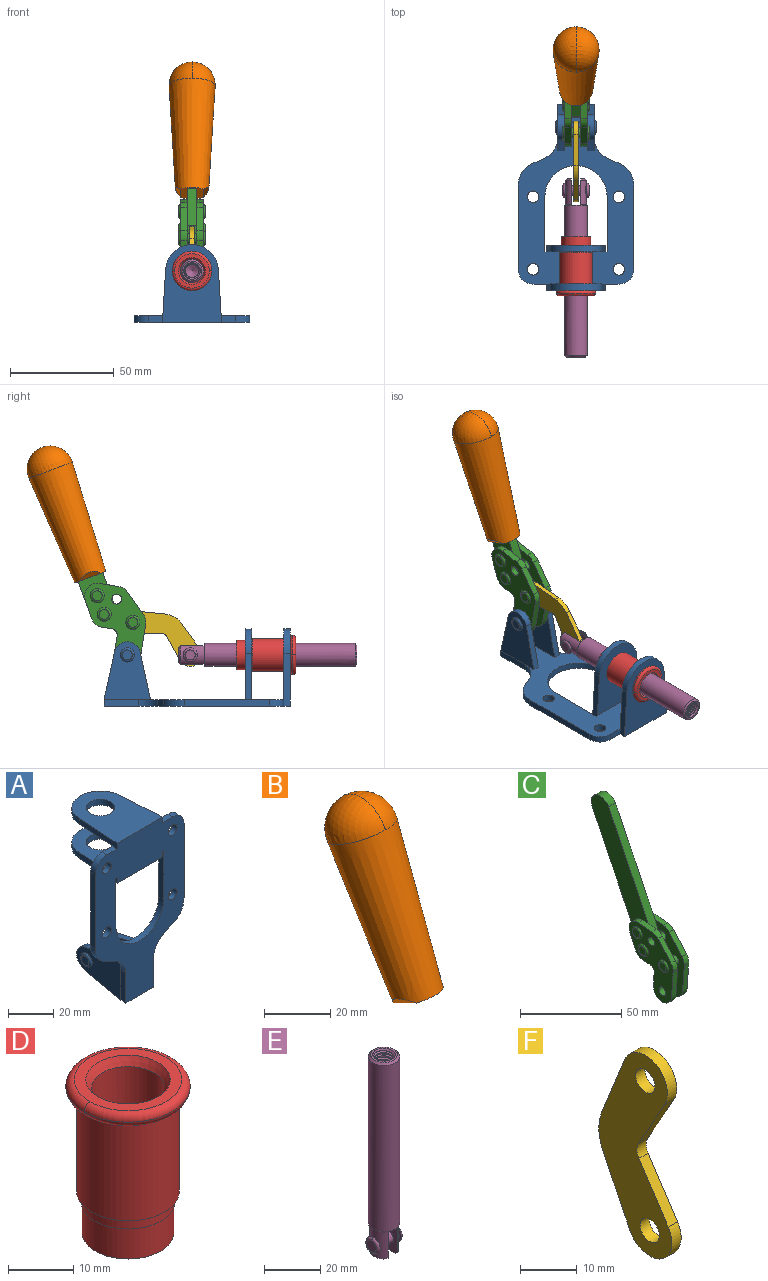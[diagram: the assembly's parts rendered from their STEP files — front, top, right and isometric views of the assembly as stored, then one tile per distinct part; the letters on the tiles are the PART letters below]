
ASSEMBLY  parts=6 mates=6
PART A: 55 faces, bbox 55.7x37.4x89.8 mm
  f0: torus R=2.41mm, axis (-1,0,0), area 15mm2, adj f11,f15,f25
  f1: torus R=2.41mm, axis (-1,0,0), area 15mm2, adj f10,f12,f22
  f2: cylinder r=2.78mm len=5.56mm, axis (0,-1,0), area 54.2mm2, adj f30,f54
  f3: cylinder r=14.99mm len=29.97mm, axis (0,-1,0), area 145.9mm2, adj f30,f49,f53,f54
  f4: cylinder r=2.78mm len=5.56mm, axis (0,-1,0), area 54.2mm2, adj f30,f54
  f5: cylinder r=2.78mm len=5.56mm, axis (0,-1,0), area 54.2mm2, adj f30,f54
  f6: cylinder r=2.78mm len=5.56mm, axis (0,-1,0), area 54.2mm2, adj f30,f54
  f7: cylinder r=6.35mm len=12.7mm, axis (0,0,1), area 123.6mm2, adj f27,f51
  f8: cylinder r=6.35mm len=12.7mm, axis (0,0,-1), area 124.7mm2, adj f21,f35
  f9: cylinder r=2.41mm len=11.18mm, axis (-1,0,0), area 169.4mm2, adj f16,f19
  f10: plane 4.83x4.83mm, normal (1,0,0), area 18.3mm2, adj f1,f12
  f11: plane 4.83x4.83mm, normal (-1,0,0), area 18.3mm2, adj f0,f15
  f12: torus R=2.41mm, axis (-1,0,0), area 15mm2, adj f1,f10,f22
  f13: cylinder r=6.35mm len=12.41mm, axis (1,0,0), area 53.4mm2, adj f18,f19,f22,f23
  f14: cylinder r=6.35mm len=12.41mm, axis (-1,0,0), area 53.4mm2, adj f16,f17,f24,f25
  f15: torus R=2.41mm, axis (-1,0,0), area 15mm2, adj f0,f11,f25
  f16: plane 27.86x22.35mm, normal (1,0,0), area 425.4mm2, adj f9,f14,f17,f24,f30
  f17: plane 22.86x4.97mm, normal (0,0.21,0.98), area 72.5mm2, adj f14,f16,f25,f30
  f18: plane 22.86x4.97mm, normal (0,0.21,0.98), area 72.5mm2, adj f13,f19,f22,f30
  f19: plane 27.86x22.35mm, normal (-1,0,0), area 425.4mm2, adj f9,f13,f18,f23,f30
  f20: cylinder r=12.7mm len=25.35mm, axis (0,0,-1), area 119.8mm2, adj f21,f34,f35,f36
  f21: plane 34.21x28.07mm, normal (0,0,-1), area 702.4mm2, adj f8,f20,f30,f34,f36
  f22: plane 27.96x22.45mm, normal (1,0,0), area 407.2mm2, adj f1,f12,f13,f18,f23,f30,f42,f43
  f23: plane 22.86x4.97mm, normal (0,0.21,-0.98), area 72.5mm2, adj f13,f19,f22,f44
  f24: plane 22.86x4.97mm, normal (0,0.21,-0.98), area 72.5mm2, adj f14,f16,f25,f44
  f25: plane 27.86x22.35mm, normal (-1,0,0), area 407.1mm2, adj f0,f14,f15,f17,f24,f30,f45,f46
  f26: plane 3.1x0.95mm, normal (0,0,-1), area 2.7mm2, adj f30,f49,f50,f54
  f27: plane 34.21x28.07mm, normal (0,0,1), area 702.4mm2, adj f7,f28,f30,f50,f52
  f28: cylinder r=12.7mm len=25.35mm, axis (0,0,1), area 118.8mm2, adj f27,f50,f51,f52
  f29: plane 3.1x0.95mm, normal (0,0,-1), area 2.7mm2, adj f30,f52,f53,f54
  f30: plane 86.54x55.63mm, normal (0,1,0), area 2362.9mm2, adj f2,f3,f4,f5,f6,f16,f17,f18
  f31: plane 40.56x3.1mm, normal (-1,0,0), area 125.7mm2, adj f30,f32,f48,f54
  f32: cylinder r=7.11mm len=7.11mm, axis (0,-1,0), area 34.6mm2, adj f30,f31,f33,f54
  f33: plane 6.67x3.1mm, normal (0,0,1), area 20.4mm2, adj f30,f32,f34,f54
  f34: plane 25.39x3.13mm, normal (-1,0.06,0), area 79.5mm2, adj f20,f21,f33,f35,f54
  f35: plane 37.31x28.45mm, normal (0,0,1), area 789.9mm2, adj f8,f20,f34,f36,f54
  f36: plane 25.39x3.13mm, normal (1,0.06,0), area 79.5mm2, adj f20,f21,f35,f37,f54
  f37: plane 6.67x3.1mm, normal (0,0,1), area 20.4mm2, adj f30,f36,f38,f54
  f38: cylinder r=7.11mm len=7.11mm, axis (0,-1,0), area 34.6mm2, adj f30,f37,f39,f54
  f39: plane 40.56x3.1mm, normal (1,0,0), area 125.7mm2, adj f30,f38,f40,f54
  f40: cylinder r=11.18mm len=10.16mm, axis (0,-1,0), area 39.5mm2, adj f30,f39,f41,f54
  f41: plane 6.09x3.1mm, normal (0.42,0,-0.91), area 20.8mm2, adj f30,f40,f42,f54
  f42: cylinder r=11.18mm len=9.41mm, axis (0,-1,0), area 37.2mm2, adj f22,f30,f41,f43,f54
  f43: plane 16.5x3.1mm, normal (1,0,0), area 51.1mm2, adj f22,f42,f44,f54
  f44: plane 17.37x3.1mm, normal (0,0,-1), area 53.8mm2, adj f23,f24,f30,f43,f45,f54
  f45: plane 16.5x3.1mm, normal (-1,0,0), area 51.1mm2, adj f25,f44,f46,f54
  f46: cylinder r=11.18mm len=9.41mm, axis (0,-1,0), area 37.2mm2, adj f25,f30,f45,f47,f54
  f47: plane 6.09x3.1mm, normal (-0.42,0,-0.91), area 20.8mm2, adj f30,f46,f48,f54
  f48: cylinder r=11.18mm len=10.16mm, axis (0,-1,0), area 39.5mm2, adj f30,f31,f47,f54
  f49: plane 26.54x3.1mm, normal (-1,0,0), area 82.3mm2, adj f3,f26,f30,f54
  f50: plane 25.39x3.1mm, normal (1,0.06,0), area 78.8mm2, adj f26,f27,f28,f51,f54
  f51: plane 37.31x28.45mm, normal (0,0,-1), area 789.9mm2, adj f7,f28,f50,f52,f54
  f52: plane 25.39x3.1mm, normal (-1,0.06,0), area 78.8mm2, adj f27,f28,f29,f51,f54
  f53: plane 26.54x3.1mm, normal (1,0,0), area 82.3mm2, adj f3,f29,f30,f54
  f54: plane 89.66x55.63mm, normal (0,-1,0), area 2678.5mm2, adj f2,f3,f4,f5,f6,f26,f29,f31
PART B: 11 faces, bbox 22.3x42.6x64.5 mm
  f0: sphere r=11.13mm, area 411.4mm2, adj f1,f8
  f1: cone r=11.11mm half-angle=3.3deg, axis (0,0.44,0.9), area 3251.8mm2, adj f0,f7,f8,f9,f10
  f2: cylinder r=6.16mm len=11.7mm, axis (1,0,0), area 89.5mm2, adj f3,f4,f5,f6
  f3: plane 60.23x36.75mm, normal (-1,0,0), area 763.6mm2, adj f2,f4,f6,f10
  f4: plane 51.37x25.05mm, normal (0,0.9,-0.44), area 264.2mm2, adj f2,f3,f5,f10
  f5: plane 60.23x36.75mm, normal (1,0,0), area 763.6mm2, adj f2,f4,f6,f10
  f6: plane 51.37x25.05mm, normal (0,-0.9,0.44), area 264.2mm2, adj f2,f3,f5,f10
  f7: plane 9.95x5.95mm, normal (0.71,-0.31,-0.64), area 25.8mm2, adj f1,f10
  f8: sphere r=11.13mm, area 411.4mm2, adj f0,f1
  f9: plane 9.95x5.95mm, normal (-0.71,-0.31,-0.64), area 25.8mm2, adj f1,f10
  f10: plane 14.27x11.38mm, normal (0,-0.44,-0.9), area 106.7mm2, adj f1,f3,f4,f5,f6,f7,f9
PART C: 59 faces, bbox 12.9x60.2x99.6 mm
  f0: torus R=2.39mm, axis (-1,0,0), area 14.9mm2, adj f20,f43,f51
  f1: torus R=2.39mm, axis (-1,0,0), area 14.9mm2, adj f19,f42,f51
  f2: torus R=2.39mm, axis (-1,0,0), area 14.9mm2, adj f18,f35,f51
  f3: torus R=2.39mm, axis (-1,0,0), area 14.9mm2, adj f14,f17,f23
  f4: torus R=2.39mm, axis (-1,0,0), area 14.9mm2, adj f13,f16,f23
  f5: torus R=2.39mm, axis (-1,0,0), area 14.9mm2, adj f12,f15,f23
  f6: cylinder r=2.39mm len=4.78mm, axis (1,0,0), area 46.5mm2, adj f48,f50,f51
  f7: cylinder r=2.39mm len=4.78mm, axis (1,0,0), area 46.5mm2, adj f50,f51
  f8: cylinder r=6.35mm len=12.68mm, axis (1,0,0), area 61.8mm2, adj f38,f39,f50,f51
  f9: cylinder r=2.39mm len=4.78mm, axis (-1,0,0), area 70.5mm2, adj f46,f50
  f10: cylinder r=2.39mm len=4.78mm, axis (-1,0,0), area 46.5mm2, adj f23,f45,f46
  f11: cylinder r=2.39mm len=4.78mm, axis (-1,0,0), area 46.5mm2, adj f23,f46
  f12: plane 4.78x4.78mm, normal (1,0,0), area 17.9mm2, adj f5,f15
  f13: plane 4.78x4.78mm, normal (1,0,0), area 17.9mm2, adj f4,f16
  f14: plane 4.78x4.78mm, normal (1,0,0), area 17.9mm2, adj f3,f17
  f15: torus R=2.39mm, axis (-1,0,0), area 14.9mm2, adj f5,f12,f23
  f16: torus R=2.39mm, axis (-1,0,0), area 14.9mm2, adj f4,f13,f23
  f17: torus R=2.39mm, axis (-1,0,0), area 14.9mm2, adj f3,f14,f23
  f18: plane 4.78x4.78mm, normal (-1,0,0), area 17.9mm2, adj f2,f35
  f19: plane 4.78x4.78mm, normal (-1,0,0), area 17.9mm2, adj f1,f42
  f20: plane 4.78x4.78mm, normal (-1,0,0), area 17.9mm2, adj f0,f43
  f21: plane 2.26x0.2mm, normal (1,0,0), area 0.2mm2, adj f31,f44
  f22: plane 2.26x0.2mm, normal (-1,0,0), area 0.2mm2, adj f41,f44
  f23: plane 39.37x30.77mm, normal (1,0,0), area 565.5mm2, adj f3,f4,f5,f10,f11,f15,f16,f17
  f24: cylinder r=6.1mm len=4.15mm, axis (-1,0,0), area 14.7mm2, adj f23,f25,f32,f46
  f25: plane 10.25x9.01mm, normal (0,-0.75,0.66), area 42.3mm2, adj f23,f24,f26,f46
  f26: cylinder r=6.35mm len=4.64mm, axis (-1,0,0), area 15.6mm2, adj f23,f25,f27,f46
  f27: plane 15.84x3.1mm, normal (0,-1,-0.07), area 49.2mm2, adj f23,f26,f28,f46
  f28: cylinder r=6.35mm len=12.68mm, axis (-1,0,0), area 61.8mm2, adj f23,f27,f29,f46
  f29: plane 8.11x3.1mm, normal (0,1,0.07), area 25.2mm2, adj f23,f28,f30,f46
  f30: cylinder r=3.05mm len=3.25mm, axis (-1,0,0), area 14.8mm2, adj f23,f29,f31,f46
  f31: plane 5.99x3.1mm, normal (0,0.07,-1), area 18.6mm2, adj f21,f23,f30,f44,f46
  f32: plane 9.5x3.1mm, normal (0,-0.07,1), area 29.5mm2, adj f23,f24,f33,f46,f47
  f33: cylinder r=6.1mm len=8.63mm, axis (-1,0,0), area 39.1mm2, adj f23,f32,f34,f47
  f34: plane 8.65x3.96mm, normal (0,0.91,-0.42), area 29.5mm2, adj f23,f33,f44,f47
  f35: torus R=2.39mm, axis (-1,0,0), area 14.9mm2, adj f2,f18,f51
  f36: plane 10.25x9.01mm, normal (0,-0.75,0.66), area 42.3mm2, adj f37,f49,f50,f51
  f37: cylinder r=6.35mm len=4.64mm, axis (1,0,0), area 15.6mm2, adj f36,f38,f50,f51
  f38: plane 15.84x3.1mm, normal (0,-1,-0.07), area 49.2mm2, adj f8,f37,f50,f51
  f39: plane 8.11x3.1mm, normal (0,1,0.07), area 25.2mm2, adj f8,f40,f50,f51
  f40: cylinder r=3.05mm len=3.25mm, axis (1,0,0), area 14.8mm2, adj f39,f41,f50,f51
  f41: plane 5.99x3.1mm, normal (0,0.07,-1), area 18.6mm2, adj f22,f40,f44,f50,f51
  f42: torus R=2.39mm, axis (-1,0,0), area 14.9mm2, adj f1,f19,f51
  f43: torus R=2.39mm, axis (-1,0,0), area 14.9mm2, adj f0,f20,f51
  f44: cylinder r=6.35mm len=12.12mm, axis (-1,0,0), area 128.9mm2, adj f21,f22,f23,f31,f34,f41,f46,f47
  f45: plane 2.65x1.35mm, normal (1,0,0), area 1mm2, adj f10,f55
  f46: plane 39.08x20.42mm, normal (-1,0,0), area 412.5mm2, adj f9,f10,f11,f24,f25,f26,f27,f28
  f47: plane 77.62x39.82mm, normal (1,0,0), area 850mm2, adj f32,f33,f34,f44,f53,f54,f55
  f48: plane 2.65x1.35mm, normal (-1,0,0), area 1mm2, adj f6,f55
  f49: cylinder r=6.1mm len=4.15mm, axis (1,0,0), area 14.7mm2, adj f36,f50,f51,f56
  f50: plane 39.08x20.42mm, normal (1,0,0), area 412.5mm2, adj f6,f7,f8,f9,f36,f37,f38,f39
  f51: plane 39.37x30.77mm, normal (-1,0,0), area 565.5mm2, adj f0,f1,f2,f6,f7,f8,f35,f36
  f52: plane 8.65x3.96mm, normal (0,0.91,-0.42), area 29.5mm2, adj f44,f51,f57,f58
  f53: plane 68.49x33.4mm, normal (0,0.9,-0.44), area 358.1mm2, adj f44,f47,f54,f58
  f54: cylinder r=6.35mm len=12.06mm, axis (1,0,0), area 93.7mm2, adj f47,f53,f55,f58
  f55: plane 68.49x33.4mm, normal (0,-0.9,0.44), area 358.1mm2, adj f44,f45,f46,f47,f48,f50,f54,f58
  f56: plane 9.5x3.1mm, normal (0,-0.07,1), area 29.5mm2, adj f49,f50,f51,f57,f58
  f57: cylinder r=6.1mm len=8.63mm, axis (1,0,0), area 39.1mm2, adj f51,f52,f56,f58
  f58: plane 77.62x39.82mm, normal (-1,0,0), area 850mm2, adj f44,f52,f53,f54,f55,f56,f57
PART D: 15 faces, bbox 20.6x20.6x28.7 mm
  f0: torus R=8.26mm, axis (0,0,1), area 56.8mm2, adj f1,f10,f12
  f1: torus R=8.26mm, axis (0,0,1), area 56.8mm2, adj f0,f6,f13
  f2: cylinder r=5.59mm len=25.91mm, axis (0,0,1), area 909.6mm2, adj f3,f4
  f3: cone r=6.86mm half-angle=45deg, axis (0,0,-1), area 70.2mm2, adj f2,f14
  f4: cone r=6.47mm half-angle=30deg, axis (0,0,1), area 66.7mm2, adj f2,f13
  f5: cylinder r=7.04mm len=14.07mm, axis (0,0,1), area 252.6mm2, adj f11,f14
  f6: torus R=8.26mm, axis (0,0,1), area 56.8mm2, adj f1,f12,f13
  f7: cylinder r=7.16mm len=14.33mm, axis (0,0,1), area 91.5mm2, adj f9,f11
  f8: cylinder r=7.86mm len=18.42mm, axis (0,0,1), area 909.6mm2, adj f9,f10
  f9: plane 15.72x15.72mm, normal (0,0,-1), area 33mm2, adj f7,f8
  f10: plane 16.51x16.51mm, normal (0,0,-1), area 19.9mm2, adj f0,f8,f12
  f11: plane 14.33x14.33mm, normal (0,0,-1), area 5.7mm2, adj f5,f7
  f12: torus R=8.26mm, axis (0,0,1), area 56.8mm2, adj f0,f6,f10
  f13: plane 16.51x16.51mm, normal (0,0,1), area 82.7mm2, adj f1,f4,f6
  f14: plane 14.07x14.07mm, normal (0,0,-1), area 7.8mm2, adj f3,f5
PART E: 48 faces, bbox 12.6x11.1x86.1 mm
  f0: torus R=2.41mm, axis (-1,0,0), area 15mm2, adj f30,f32,f34
  f1: torus R=2.41mm, axis (-1,0,0), area 15mm2, adj f29,f31,f33
  f2: cylinder r=5.54mm len=72.39mm, axis (0,0,1), area 2518.5mm2, adj f3,f4,f42,f43
  f3: cone r=5.54mm half-angle=45deg, axis (0,0,1), area 7.6mm2, adj f2,f5,f41
  f4: cone r=5.54mm half-angle=45deg, axis (0,0,-1), area 34.9mm2, adj f2,f39
  f5: cylinder r=5.08mm len=11.48mm, axis (0,0,1), area 108.3mm2, adj f3,f7,f8,f41
  f6: cylinder r=2.41mm len=4.83mm, axis (-1,0,0), area 71.2mm2, adj f40,f41
  f7: cylinder r=2.41mm len=4.83mm, axis (-1,0,0), area 7.6mm2, adj f5,f34
  f8: cone r=5.08mm half-angle=45deg, axis (0,0,1), area 10.6mm2, adj f5,f37,f41
  f9: cone r=3.98mm half-angle=45deg, axis (0,0,1), area 17.6mm2, adj f27,f39,f45,f46,f47
  f10: cylinder r=2.41mm len=4.83mm, axis (-1,0,0), area 7.6mm2, adj f33,f38
  f11: cylinder r=3.2mm len=6.4mm, axis (0,0,1), area 78.4mm2, adj f12,f28,f44,f45,f47
  f12: cylinder r=3.2mm len=6.4mm, axis (0,0,1), area 10.5mm2, adj f11,f13,f45,f47
  f13: cylinder r=3.2mm len=6.4mm, axis (0,0,1), area 10.5mm2, adj f12,f14,f45,f47
  f14: cylinder r=3.2mm len=6.4mm, axis (0,0,1), area 10.5mm2, adj f13,f15,f45,f47
  f15: cylinder r=3.2mm len=6.4mm, axis (0,0,1), area 10.5mm2, adj f14,f16,f45,f47
  f16: cylinder r=3.2mm len=6.4mm, axis (0,0,1), area 10.5mm2, adj f15,f17,f45,f47
  f17: cylinder r=3.2mm len=6.4mm, axis (0,0,1), area 10.5mm2, adj f16,f18,f45,f47
  f18: cylinder r=3.2mm len=6.4mm, axis (0,0,1), area 10.5mm2, adj f17,f19,f45,f47
  f19: cylinder r=3.2mm len=6.4mm, axis (0,0,1), area 10.5mm2, adj f18,f20,f45,f47
  f20: cylinder r=3.2mm len=6.4mm, axis (0,0,1), area 10.5mm2, adj f19,f21,f45,f47
  f21: cylinder r=3.2mm len=6.4mm, axis (0,0,1), area 10.5mm2, adj f20,f22,f45,f47
  f22: cylinder r=3.2mm len=6.4mm, axis (0,0,1), area 10.5mm2, adj f21,f23,f45,f47
  f23: cylinder r=3.2mm len=6.4mm, axis (0,0,1), area 10.5mm2, adj f22,f24,f45,f47
  f24: cylinder r=3.2mm len=6.4mm, axis (0,0,1), area 10.5mm2, adj f23,f25,f45,f47
  f25: cylinder r=3.2mm len=6.4mm, axis (0,0,1), area 10.5mm2, adj f24,f26,f45,f47
  f26: cylinder r=3.2mm len=6.4mm, axis (0,0,1), area 10.5mm2, adj f25,f27,f45,f47
  f27: cylinder r=3.2mm len=6.4mm, axis (0,0,1), area 7.4mm2, adj f9,f26,f45,f47
  f28: cone r=3.2mm half-angle=60deg, axis (0,0,1), area 37.2mm2, adj f11
  f29: plane 4.83x4.83mm, normal (-1,0,0), area 18.3mm2, adj f1,f31
  f30: plane 4.83x4.83mm, normal (1,0,0), area 18.3mm2, adj f0,f32
  f31: torus R=2.41mm, axis (-1,0,0), area 15mm2, adj f1,f29,f33
  f32: torus R=2.41mm, axis (-1,0,0), area 15mm2, adj f0,f30,f34
  f33: plane 6.83x6.83mm, normal (1,0,0), area 18.3mm2, adj f1,f10,f31
  f34: plane 6.83x6.83mm, normal (-1,0,0), area 18.3mm2, adj f0,f7,f32
  f35: cone r=5.08mm half-angle=45deg, axis (0,0,1), area 10.6mm2, adj f36,f38,f40
  f36: plane 7.25x1.97mm, normal (0,0,-1), area 10mm2, adj f35,f40
  f37: plane 7.25x1.97mm, normal (0,0,-1), area 10mm2, adj f8,f41
  f38: cylinder r=5.08mm len=11.48mm, axis (0,0,1), area 108.3mm2, adj f10,f35,f40,f42
  f39: plane 9.55x9.55mm, normal (0,0,1), area 22mm2, adj f4,f9
  f40: plane 12.76x10.09mm, normal (1,0,0), area 95.7mm2, adj f6,f35,f36,f38,f42,f43
  f41: plane 12.76x10.09mm, normal (-1,0,0), area 95.7mm2, adj f3,f5,f6,f8,f37,f43
  f42: cone r=5.54mm half-angle=45deg, axis (0,0,1), area 7.6mm2, adj f2,f38,f40
  f43: plane 11.07x4.7mm, normal (0,0,-1), area 50.4mm2, adj f2,f40,f41
  f44: plane 0.89x0.62mm, normal (-1,0,0), area 0.3mm2, adj f11,f45,f46,f47
  f45: bspline ~24.8x7.63mm, area 266.6mm2, adj f9,f11,f12,f13,f14,f15,f16,f17
  f46: bspline ~24.87x7.63mm, area 73.6mm2, adj f9,f44,f45,f47
  f47: bspline ~24.98x7.63mm, area 272.5mm2, adj f9,f11,f12,f13,f14,f15,f16,f17
PART F: 12 faces, bbox 2.3x18.2x42.8 mm
  f0: cylinder r=2.4mm len=4.8mm, axis (1,0,0), area 34.9mm2, adj f4,f11
  f1: cylinder r=10.41mm len=8.47mm, axis (1,0,0), area 20.2mm2, adj f4,f9,f10,f11
  f2: cylinder r=3.05mm len=3.16mm, axis (1,0,0), area 7.7mm2, adj f4,f6,f7,f11
  f3: cylinder r=2.4mm len=4.8mm, axis (1,0,0), area 34.9mm2, adj f4,f11
  f4: plane 42.81x18.23mm, normal (-1,0,0), area 414.1mm2, adj f0,f1,f2,f3,f5,f6,f7,f8
  f5: cylinder r=5.54mm len=10.67mm, axis (1,0,0), area 41.8mm2, adj f4,f6,f10,f11
  f6: plane 11.66x6.53mm, normal (0,-0.87,-0.49), area 30.9mm2, adj f2,f4,f5,f11
  f7: plane 11.17x7.33mm, normal (0,-0.84,0.55), area 30.9mm2, adj f2,f4,f8,f11
  f8: cylinder r=5.54mm len=10.51mm, axis (1,0,0), area 41.8mm2, adj f4,f7,f9,f11
  f9: plane 13.67x6.67mm, normal (0,0.9,-0.44), area 35.1mm2, adj f1,f4,f8,f11
  f10: plane 14.1x5.7mm, normal (0,0.93,0.37), area 35.1mm2, adj f1,f4,f5,f11
  f11: plane 42.81x18.23mm, normal (1,0,0), area 414.1mm2, adj f0,f1,f2,f3,f5,f6,f7,f8
PLACE A rot(axis=(1,0,0),90deg) t=(4.44,6.88,-6.04)mm fixed
PLACE B rot(axis=(1,0,0),5.6deg) t=(4.48,11.34,48.1)mm
PLACE C rot(axis=(1,0,0),5.6deg) t=(4.44,11.34,48.1)mm
PLACE D rot(axis=(1,0,0),90deg) t=(4.44,6.88,-6.04)mm
PLACE E rot(axis=(1,0,0),90deg) t=(4.44,24.17,-6.04)mm
PLACE F rot(axis=(1,0,0),121.5deg) t=(4.44,34.76,5.69)mm
MATE revolute F.f3 <-> C.f4  axis (1,0,0) through (4.44,36.32,34.22)mm
MATE revolute F.f5 <-> E.f6  axis (1,0,0) through (4.44,8.7,18.57)mm
MATE fastened A.f7 <-> D.f0  axis (0,-1,0) through (4.44,-39.51,18.57)mm
MATE slider E.f2 <-> A.f7  axis (0,-1,0) through (4.44,-34.61,18.57)mm
MATE revolute C.f7 <-> A.f0  axis (1,0,0) through (4.44,38.98,18.57)mm
MATE fastened B.f2 <-> C.f54  axis (-1,0,0) through (6.79,76.67,109.57)mm
